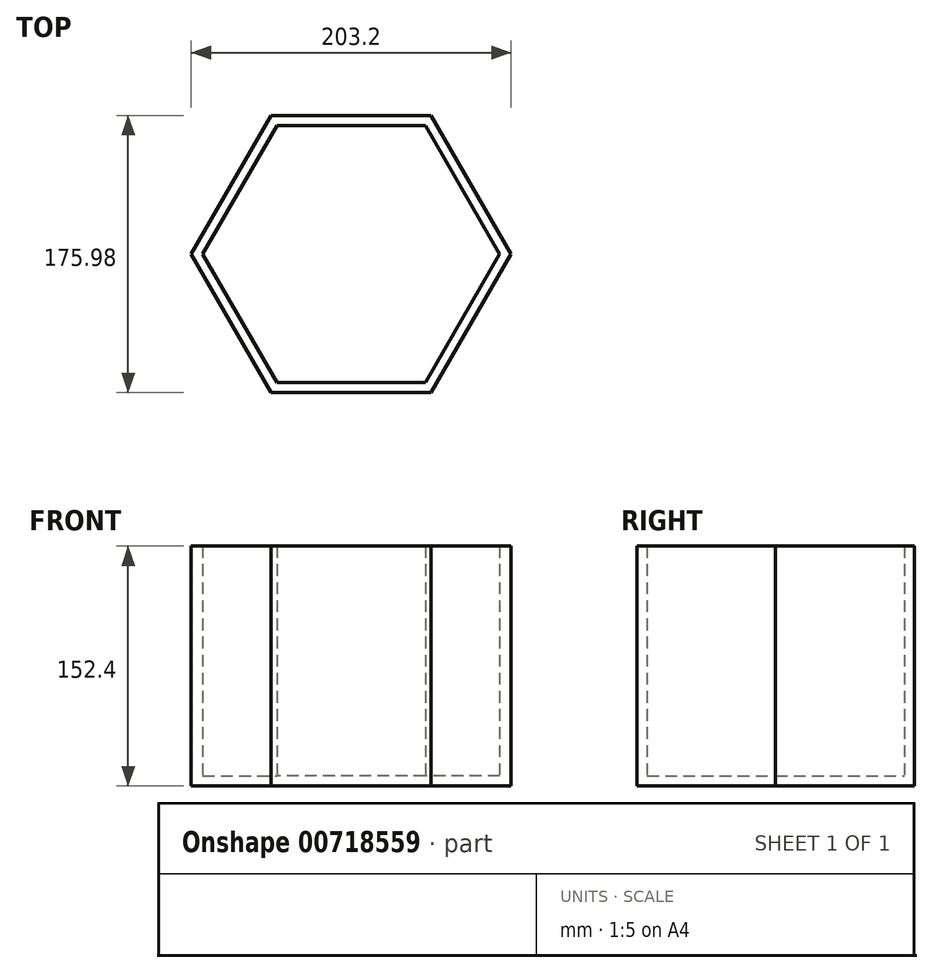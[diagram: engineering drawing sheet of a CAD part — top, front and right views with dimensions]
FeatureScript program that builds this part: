
annotation { "Feature Type Name" : "Feature", "Feature Type Description" : "" }
export const myFeature = defineFeature(function(context is Context, id is Id, definition is map)
    precondition{}
    {
        {
            var Q0;
            Q0=qCreatedBy(makeId("Top.planeOp"),FACE);
            var sketch = newSketch(context, id + "F0", { "sketchPlane" : qUnion([Q0])});
            skLineSegment(sketch, "E0", {"start": v(-101.6, 0) * mm, "end": v(-50.8, 87.99) * mm});
            skLineSegment(sketch, "E1", {"start": v(-50.8, 87.99) * mm, "end": v(50.8, 87.99) * mm});
            skLineSegment(sketch, "E2", {"start": v(50.8, 87.99) * mm, "end": v(101.6, 0) * mm});
            skLineSegment(sketch, "E3", {"start": v(101.6, 0) * mm, "end": v(50.8, -87.99) * mm});
            skLineSegment(sketch, "E4", {"start": v(50.8, -87.99) * mm, "end": v(-50.8, -87.99) * mm});
            skLineSegment(sketch, "E5", {"start": v(-50.8, -87.99) * mm, "end": v(-101.6, 0) * mm});
            skSolve(sketch);
        }
        {
            var Q0;
            Q0=qCreatedBy(makeId("Top.planeOp"),FACE);
            var sketch = newSketch(context, id + "F1", { "sketchPlane" : qUnion([Q0])});
            skLineSegment(sketch, "E6", {"start": v(-127, 0) * mm, "end": v(-63.5, 109.99) * mm});
            skLineSegment(sketch, "E7", {"start": v(-63.5, 109.99) * mm, "end": v(63.5, 109.99) * mm});
            skLineSegment(sketch, "E8", {"start": v(63.5, 109.99) * mm, "end": v(127, 0) * mm});
            skLineSegment(sketch, "E9", {"start": v(127, 0) * mm, "end": v(63.5, -109.99) * mm});
            skLineSegment(sketch, "E10", {"start": v(63.5, -109.99) * mm, "end": v(-63.5, -109.99) * mm});
            skLineSegment(sketch, "E11", {"start": v(-63.5, -109.99) * mm, "end": v(-127, 0) * mm});
            skLineSegment(sketch, "E12.0.0", {"start": v(-101.6, 0) * mm, "end": v(-50.8, -87.99) * mm});
            skLineSegment(sketch, "E12.0.1", {"start": v(-50.8, -87.99) * mm, "end": v(50.8, -87.99) * mm});
            skLineSegment(sketch, "E12.0.2", {"start": v(50.8, -87.99) * mm, "end": v(101.6, 0) * mm});
            skLineSegment(sketch, "E12.0.3", {"start": v(101.6, 0) * mm, "end": v(50.8, 87.99) * mm});
            skLineSegment(sketch, "E12.0.4", {"start": v(50.8, 87.99) * mm, "end": v(-50.8, 87.99) * mm});
            skLineSegment(sketch, "E12.0.5", {"start": v(-50.8, 87.99) * mm, "end": v(-101.6, 0) * mm});
            skSolve(sketch);
        }
        {
            var Q0;
            Q0=makeQuery(id+"F0.imprint","IMPRINT",FACE,{"disambiguationData":[TD([[makeQuery(id+"F0.imprint","IMPRINT",EDGE,{"derivedFrom":sQuery(id+"F0.wireOp",EDGE,"E0")}),-1.0]])]});
            extrude(context, id + "F2", {"entities" : qUnion([Q0]), "depth" : 152.4 * mm, "offsetDistance" : 25.4 * mm});
        }
        {
            var Q0;
            Q0=makeQuery(id+"F2.opExtrude","CAP_FACE",FACE,{"disambiguationData":[OSD([sQuery(id+"F0.wireOp",EDGE,"E0"),sQuery(id+"F0.wireOp",EDGE,"E1"),sQuery(id+"F0.wireOp",EDGE,"E2"),sQuery(id+"F0.wireOp",EDGE,"E3"),sQuery(id+"F0.wireOp",EDGE,"E4"),sQuery(id+"F0.wireOp",EDGE,"E5")])],"isStart":false});
            shell(context, id + "F3", {"entities" : qUnion([Q0]), "thickness" : 6.35 * mm});
        }
    });
